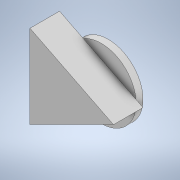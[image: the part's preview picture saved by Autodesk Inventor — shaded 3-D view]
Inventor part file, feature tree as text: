
AUTODESK INVENTOR PART (.ipt)
format: ipt  version: 2020.1 (Build 241239000, 239)  size: 106,496 bytes
history: native  units: mm
features: extrude x2, sketch x2
ambient origin geometry x8: Origin, YZ Plane, XZ Plane, XY Plane, X Axis, Y Axis, Z Axis, Center Point
bodies: Body1 (feature_tree)
feature tree (4):
  extrude  "Extrusion4"  Depth=10.0mm
  extrude  "Extrusion5"  [1 undecoded]
  sketch  "Sketch3"  dims[d12=4.25mm d13=0.0mm d16=10.0mm]
  sketch  "Sketch4"  dims[d17=1.0mm d18=0.0mm]
note: 1 required parameter value undecoded (feature->parameter linkage not recoverable at this tier; creation-order binding heuristic only, values carry confidence <= 0.55)
